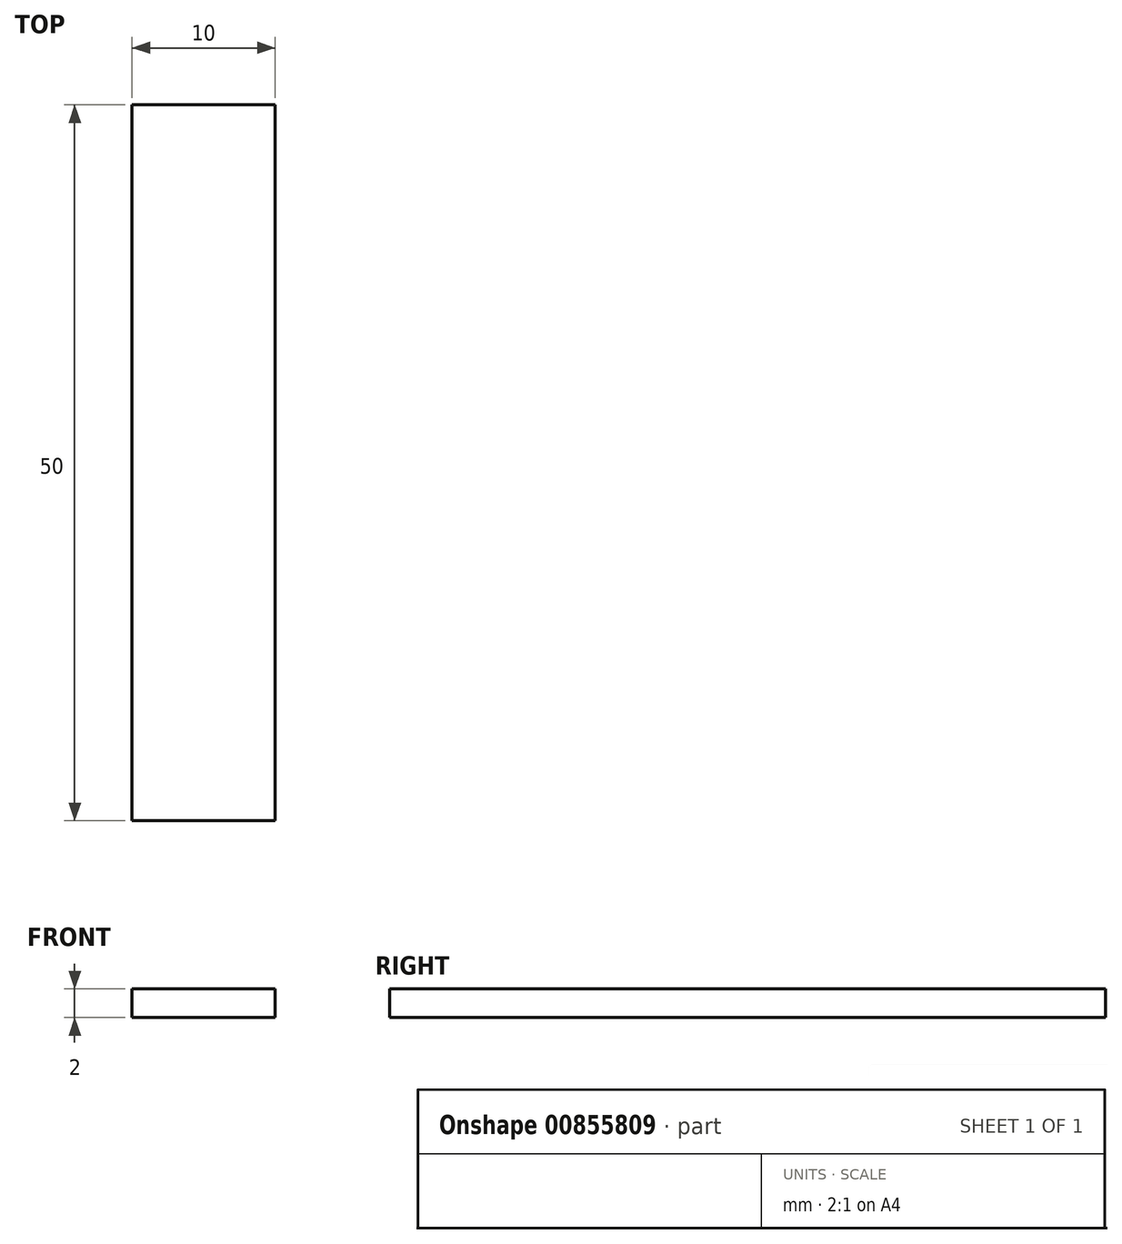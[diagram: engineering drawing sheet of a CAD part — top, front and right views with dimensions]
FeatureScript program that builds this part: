
annotation { "Feature Type Name" : "Feature", "Feature Type Description" : "" }
export const myFeature = defineFeature(function(context is Context, id is Id, definition is map)
    precondition{}
    {
        {
            var Q0;
            Q0=qCreatedBy(makeId("Front.planeOp"),FACE);
            var sketch = newSketch(context, id + "F0", { "sketchPlane" : qUnion([Q0])});
            skLineSegment(sketch, "E0.bottom", {"start": v(5, 1) * mm, "end": v(-5, 1) * mm});
            skLineSegment(sketch, "E0.top", {"start": v(5, -1) * mm, "end": v(-5, -1) * mm});
            skLineSegment(sketch, "E0.left", {"start": v(5, 1) * mm, "end": v(5, -1) * mm});
            skLineSegment(sketch, "E0.right", {"start": v(-5, 1) * mm, "end": v(-5, -1) * mm});
            skPoint(sketch, "E0.middle", {"position": v(0, 0) * mm});
            skSolve(sketch);
        }
        {
            var Q0;
            Q0=qSketchRegion(id+"F0",true);
            extrude(context, id + "F1", {"entities" : qUnion([Q0]), "depth" : 50 * mm, "offsetDistance" : 25 * mm});
        }
    });
